# Revit family: Water_Boiler-Navien-NFC-Condensing-NFC-175
name_source: partatom
category: Mechanical Equipment
revit_build: Autodesk Revit 2017 (Build: 20160720_1515(x64)
units: mm (PartAtom-declared; Revit-internal decimal feet)

## family parameters
Cut with Voids When Loaded = No
Host = Face
OmniClass Number = 23.65.35.11
OmniClass Title = Supply Water Heaters
Part Type = Normal
Room Calculation Point = No
Round Connector Dimension = Use Diameter
Shared = No

## types (1)
- NFC-175
    2" Exhaust/Intake = Yes
    3" Exhaust/Intake = No
    Apparent Load = 0 VA
    Assembly Code = D3010500
    Auto Feeder Inlet = 1/2"
    Certifications = Energy Star | AHRI | CSA | ASME | CSA Blue Star | CSA Blue Flame
    Cold Water Inlet = 1"
    Condensate Outlet = 1/2"
    Default Elevation = 48"
    Depth = 17 5/16"
    Description = Condensing Gas Hot Water Boiler
    Exhaust = 2"
    Finish = Metal - Navien - White
    Flow Rate = 0 GPM
    Frequency = 60 Hz
    Gas Connection Size = 1"
    Gas Inlet = 1"
    Heating Capacity = 175000.0 Btu/h
    Heating Capacity Note = 175,000 to 18,000 BTUh
    Heating Return = 1 1/4"
    Heating Supply = 1 1/4"
    Height = 33 1/2"
    Hot Water Outlet = 1"
    Ignition = Electronic ignition
    Installation Type = Indoor Wall-Hung
    Intake = 2"
    Keynote = 22 33 00.A1
    Manufacturer = Navien, Inc.
    Manufacturer Fax Number = (949) 420-0430
    Model = NFC-175
    Natural Gas Manifold Pressure = -0.05" to -0.47" WC
    Natural Gas Supply Pressure = 3.5" to 10.5" WC
    Number of Poles = 1
    Phase = 1
    Power Factor = 1
    Product Documentation Link = https://www.navieninc.com
    Product Name = NFC Series Combination Boilers
    Product Page URL = https://www.navieninc.com
    Propane Gas Manifold Pressure = -0.10" to -0.45" WC
    Propane Gas Supply Pressure = 8.0" to 13.5" WC
    URL = https://www.navieninc.com
    Venting = Exhaust: 2 in or 3 in PVC, CPVC, Approved Polypropylene, Stainless Steel, 2 in or 3 in Special Gas Vent Type BH (Class III, A/B/C) | Intake: 2 in or 3 in PVC, CPVC, Polypropylene, Stainless Steel, ABS 2 in or 3 in Special Gas Vent Type BH (Class III, A/B/C) | Vent Clearance: 0 in to combustibles
    Venting Type = Forced draft direct vent
    Version = 2017 - v1.0.a
    Voltage = 120 V
    Warranty = https://www.navieninc.com
    Warranty Note = Heat Exchangers: 15 years limited warranty (Residential), 10 years (Commercial) | Parts: 5 years (Residential), 3 years (Commercial)
    Water Pressure = 12–80 psi
    Weight = 145.00 lbf
    Wi-Fi Ready = NaviLink Wi‑Fi Control: This add-on accessory enables access to control temperatures remotely, access usage data and receive diagnostic notifications via smartphone or tablet.
    Width = 17 5/16"

## geometry (parser evidence)
native form markers: Sweep x6
no freeform markers — native parametric forms only
